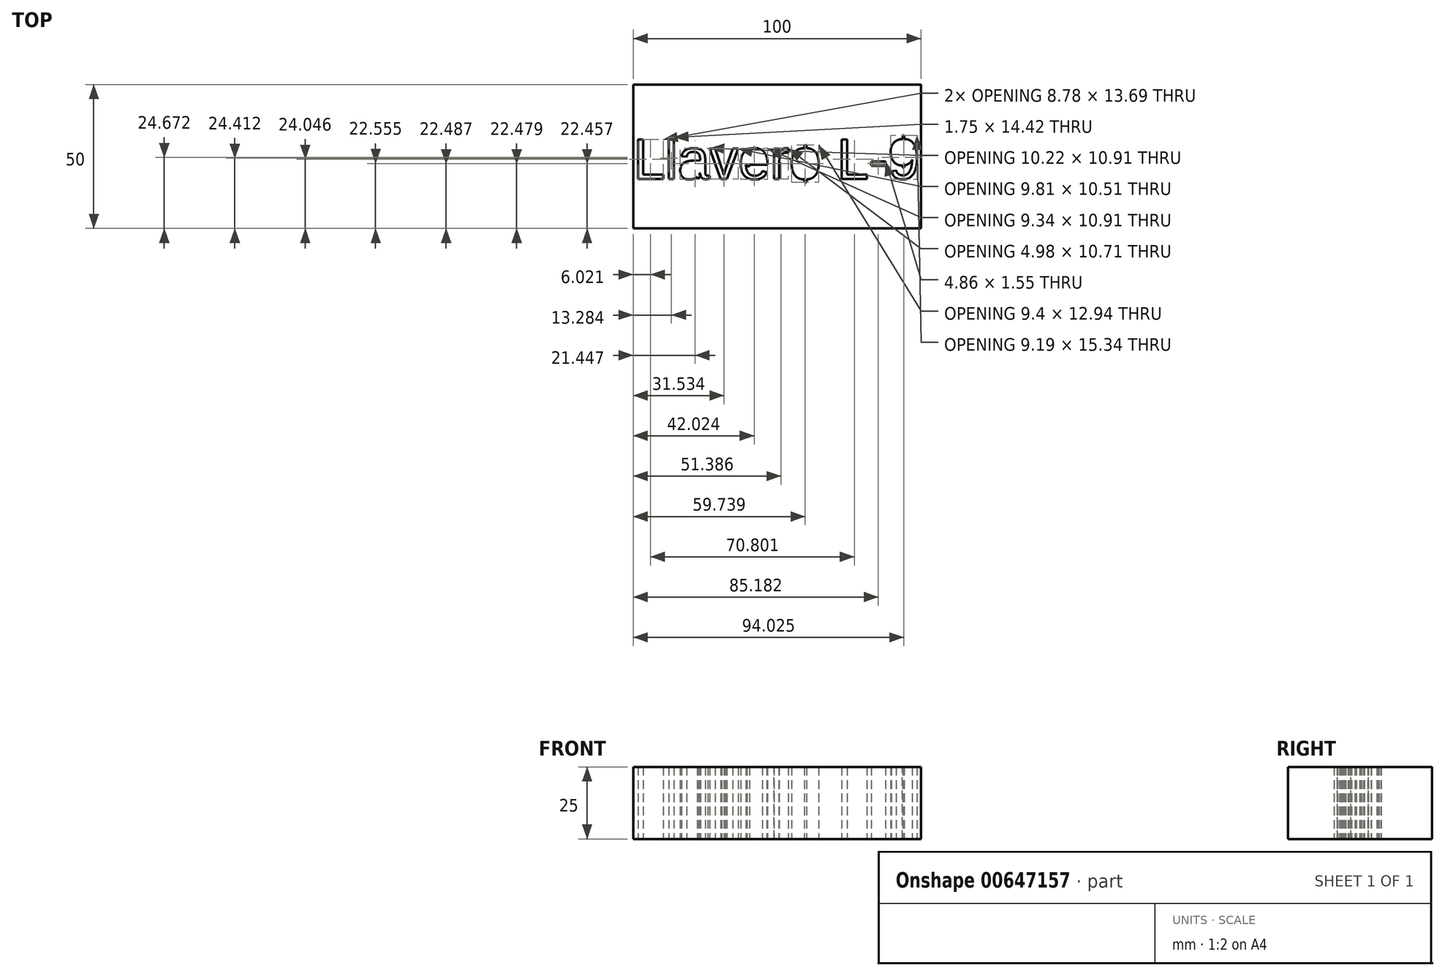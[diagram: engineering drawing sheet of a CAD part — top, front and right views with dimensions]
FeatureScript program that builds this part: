
annotation { "Feature Type Name" : "Feature", "Feature Type Description" : "" }
export const myFeature = defineFeature(function(context is Context, id is Id, definition is map)
    precondition{}
    {
        {
            var Q0;
            Q0=qCreatedBy(makeId("Top.planeOp"),FACE);
            var sketch = newSketch(context, id + "F0", { "sketchPlane" : qUnion([Q0])});
            skLineSegment(sketch, "E0.bottom", {"start": v(0, 0) * mm, "end": v(100, 0) * mm});
            skLineSegment(sketch, "E0.top", {"start": v(0, -50) * mm, "end": v(100, -50) * mm});
            skLineSegment(sketch, "E0.left", {"start": v(0, 0) * mm, "end": v(0, -50) * mm});
            skLineSegment(sketch, "E0.right", {"start": v(100, 0) * mm, "end": v(100, -50) * mm});
            skText(sketch, "E1", { "text": "Llavero L-9", "fontName": "Arimo-Regular.ttf"});
            skLineSegment(sketch, "E2", {"start": v(22.23, -29.47) * mm, "end": v(23.37, -31.93) * mm});
            skLineSegment(sketch, "E3", {"start": v(23.37, -31.93) * mm, "end": v(22.56, -32.8) * mm});
            skLineSegment(sketch, "E4", {"start": v(22.56, -32.8) * mm, "end": v(21.34, -29.47) * mm});
            skLineSegment(sketch, "E5", {"start": v(21.34, -29.47) * mm, "end": v(22.23, -29.47) * mm});
            skLineSegment(sketch, "E6", {"start": v(39.54, -26.11) * mm, "end": v(39.54, -28.3) * mm});
            skLineSegment(sketch, "E7", {"start": v(39.54, -28.3) * mm, "end": v(40.38, -28.3) * mm});
            skLineSegment(sketch, "E8", {"start": v(40.38, -28.3) * mm, "end": v(40.38, -25.96) * mm});
            skLineSegment(sketch, "E9", {"start": v(40.38, -25.96) * mm, "end": v(39.54, -26.11) * mm});
            skLineSegment(sketch, "E10", {"start": v(59.42, -21.16) * mm, "end": v(59.42, -33.99) * mm});
            skLineSegment(sketch, "E11", {"start": v(59.42, -33.99) * mm, "end": v(60.18, -33.99) * mm});
            skLineSegment(sketch, "E12", {"start": v(60.18, -33.99) * mm, "end": v(60.18, -21.05) * mm});
            skLineSegment(sketch, "E13", {"start": v(60.18, -21.05) * mm, "end": v(59.42, -21.16) * mm});
            skLineSegment(sketch, "E14", {"start": v(93.6, -17.72) * mm, "end": v(93.6, -28.84) * mm});
            skLineSegment(sketch, "E15", {"start": v(93.6, -28.84) * mm, "end": v(94.15, -28.84) * mm});
            skLineSegment(sketch, "E16", {"start": v(94.15, -28.84) * mm, "end": v(94.15, -17.66) * mm});
            skLineSegment(sketch, "E17", {"start": v(94.15, -17.66) * mm, "end": v(93.6, -17.72) * mm});
            const initialGuessF0  = {"E1": [0, -0.0328, 1, 0, 0.01433]};
            skSetInitialGuess(sketch, initialGuessF0);
            skSolve(sketch);
        }
        {
            var Q0;
            Q0=makeQuery(id+"F0.imprint","IMPRINT",FACE,{"disambiguationData":[TD([[makeQuery(id+"F0.imprint","IMPRINT",EDGE,{"derivedFrom":sQuery(id+"F0.wireOp",EDGE,"E0.bottom")}),-1.0]])]});
            extrude(context, id + "F1", {"entities" : qUnion([Q0]), "depth" : 25 * mm, "offsetDistance" : 25 * mm});
        }
    });
